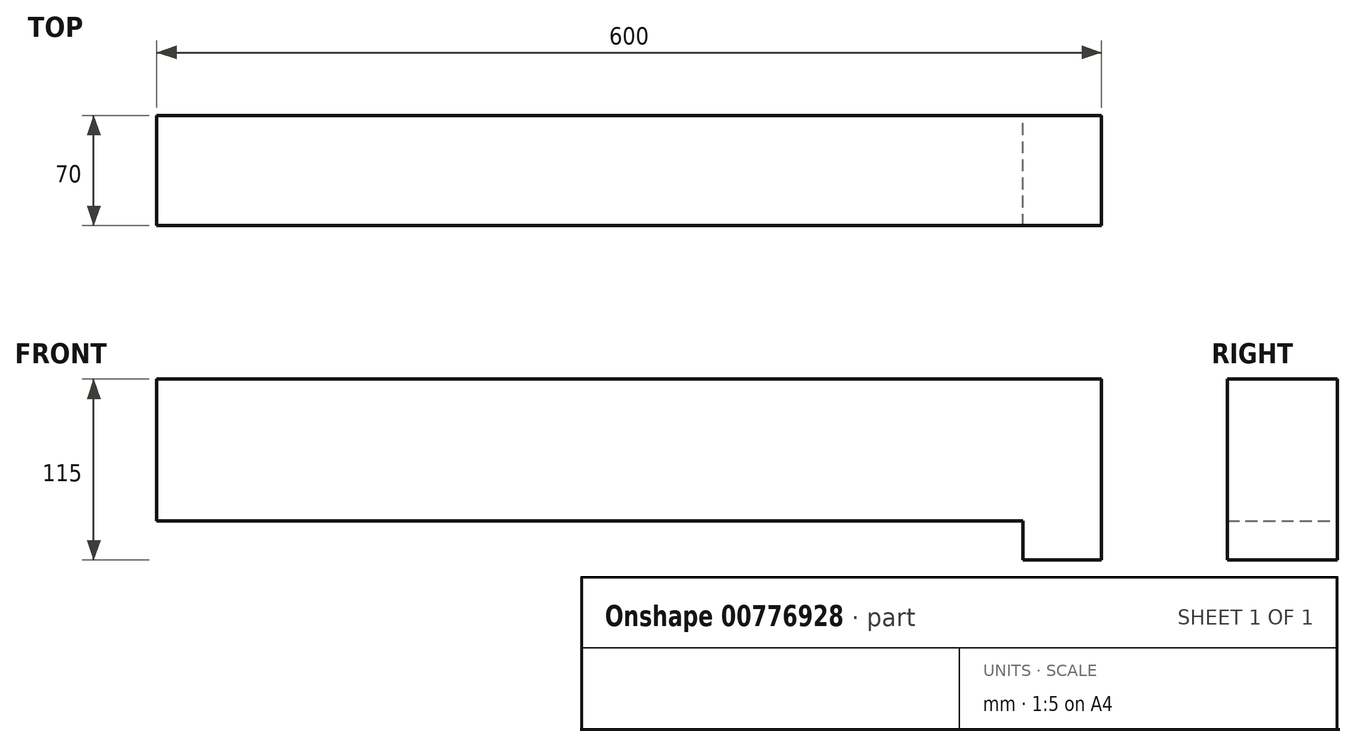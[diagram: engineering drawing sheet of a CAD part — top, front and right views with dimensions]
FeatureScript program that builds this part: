
annotation { "Feature Type Name" : "Feature", "Feature Type Description" : "" }
export const myFeature = defineFeature(function(context is Context, id is Id, definition is map)
    precondition{}
    {
        {
            var Q0;
            Q0=qCreatedBy(makeId("Right.planeOp"),FACE);
            var sketch = newSketch(context, id + "F0", { "sketchPlane" : qUnion([Q0])});
            skLineSegment(sketch, "E0.bottom", {"start": v(35, 45) * mm, "end": v(-35, 45) * mm});
            skLineSegment(sketch, "E0.top", {"start": v(35, -45) * mm, "end": v(-35, -45) * mm});
            skLineSegment(sketch, "E0.left", {"start": v(35, 45) * mm, "end": v(35, -45) * mm});
            skLineSegment(sketch, "E0.right", {"start": v(-35, 45) * mm, "end": v(-35, -45) * mm});
            skPoint(sketch, "E0.middle", {"position": v(0, 0) * mm});
            skSolve(sketch);
        }
        {
            var Q0;
            Q0 = qSketchRegion(id + "F0", true);
            extrude(context, id + "F1", {"entities" : qUnion([Q0]), "depth" : 600 * mm, "offsetDistance" : 25 * mm});
        }
        {
            var Q0;
            Q0=makeQuery(id+"F1.opExtrude","SWEPT_FACE",FACE,{"disambiguationData":[OSD([sQuery(id+"F0.wireOp",EDGE,"E0.top")])]});
            var sketch = newSketch(context, id + "F2", { "sketchPlane" : qUnion([Q0])});
            skLineSegment(sketch, "E1.bottom", {"start": v(600, 35) * mm, "end": v(550, 35) * mm});
            skLineSegment(sketch, "E1.top", {"start": v(600, -35) * mm, "end": v(550, -35) * mm});
            skLineSegment(sketch, "E1.left", {"start": v(600, 35) * mm, "end": v(600, -35) * mm});
            skLineSegment(sketch, "E1.right", {"start": v(550, 35) * mm, "end": v(550, -35) * mm});
            skSolve(sketch);
        }
        {
            var Q0;
            Q0 = qSketchRegion(id + "F2", true);
            extrude(context, id + "F3", {"entities" : qUnion([Q0]), "operationType" : NewBodyOperationType.ADD, "depth" : 25 * mm, "offsetDistance" : 25 * mm});
        }
    });
